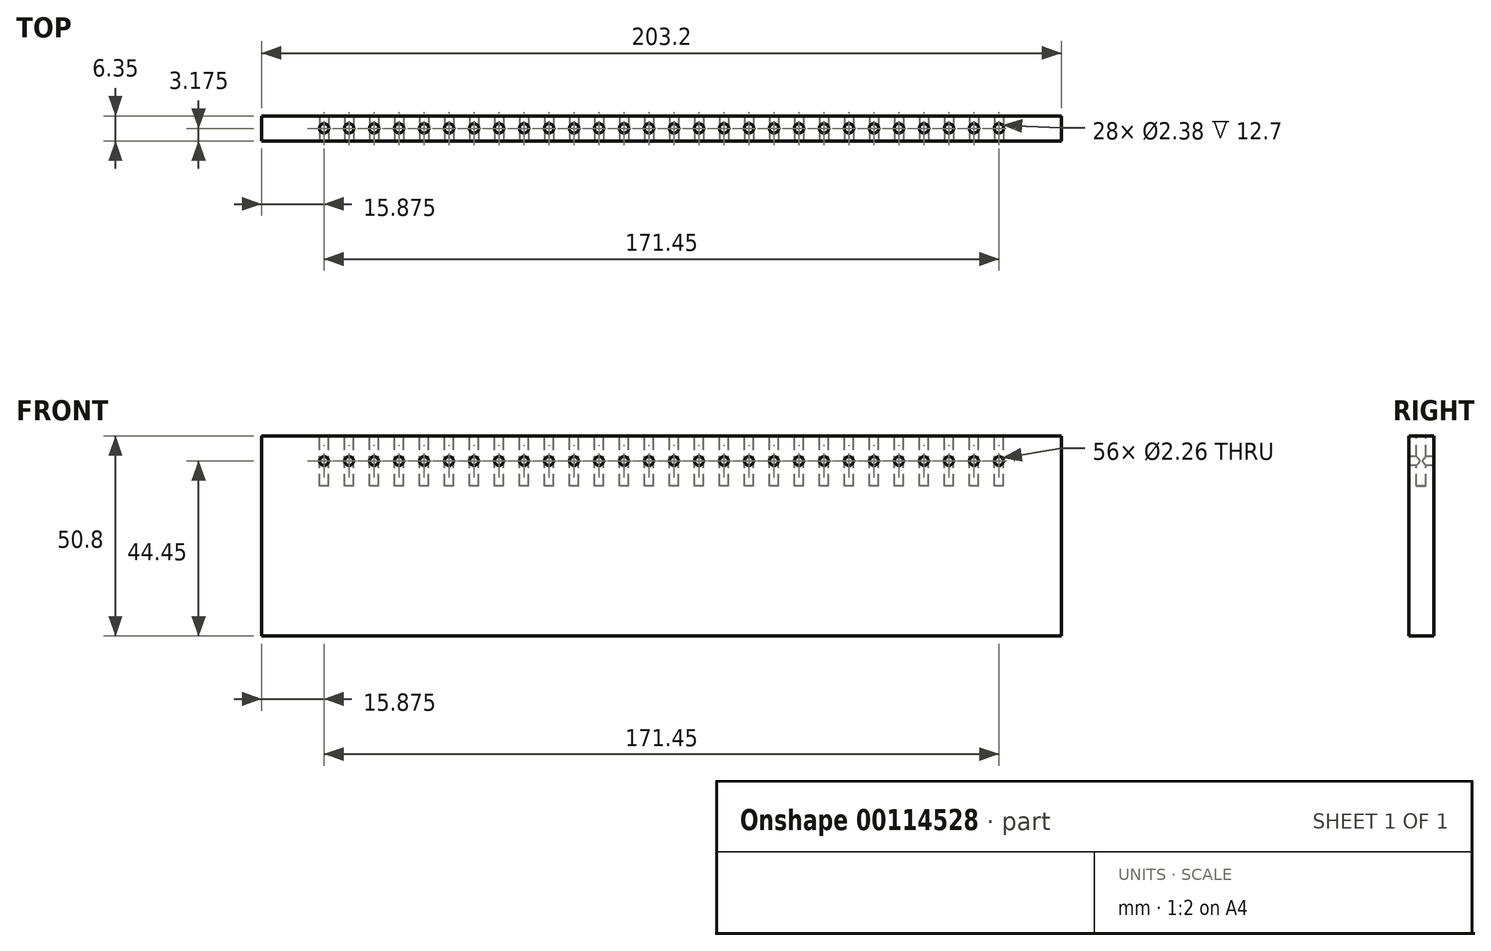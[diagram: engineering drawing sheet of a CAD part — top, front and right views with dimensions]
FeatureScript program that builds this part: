
annotation { "Feature Type Name" : "Feature", "Feature Type Description" : "" }
export const myFeature = defineFeature(function(context is Context, id is Id, definition is map)
    precondition{}
    {
        {
            var Q0;
            Q0=qCreatedBy(makeId("Front.planeOp"),FACE);
            var sketch = newSketch(context, id + "F0", { "sketchPlane" : qUnion([Q0])});
            skLineSegment(sketch, "E0.bottom", {"start": v(0, 0) * mm, "end": v(203.2, 0) * mm});
            skLineSegment(sketch, "E0.top", {"start": v(0, 50.8) * mm, "end": v(203.2, 50.8) * mm});
            skLineSegment(sketch, "E0.left", {"start": v(0, 0) * mm, "end": v(0, 50.8) * mm});
            skLineSegment(sketch, "E0.right", {"start": v(203.2, 0) * mm, "end": v(203.2, 50.8) * mm});
            skSolve(sketch);
        }
        {
            var Q0;
            Q0 = qSketchRegion(id + "F0", true);
            extrude(context, id + "F1", {"entities" : qUnion([Q0]), "depth" : 6.35 * mm});
        }
        {
            var Q0;
            Q0=makeQuery(id+"F1.opExtrude","SWEPT_FACE",FACE,{"disambiguationData":[OSD([sQuery(id+"F0.wireOp",EDGE,"E0.top")])]});
            var sketch = newSketch(context, id + "F2", { "sketchPlane" : qUnion([Q0])});
            skCircle(sketch, "E1", {"center": v(15.88, -3.18) * mm, "radius": 1.2 * mm});
            skCircle(sketch, "E2.1.0.0", {"center": v(22.23, -3.17) * mm, "radius": 1.2 * mm});
            skCircle(sketch, "E2.2.0.0", {"center": v(28.58, -3.18) * mm, "radius": 1.2 * mm});
            skCircle(sketch, "E2.3.0.0", {"center": v(34.92, -3.18) * mm, "radius": 1.2 * mm});
            skCircle(sketch, "E2.4.0.0", {"center": v(41.28, -3.18) * mm, "radius": 1.2 * mm});
            skCircle(sketch, "E2.5.0.0", {"center": v(47.62, -3.18) * mm, "radius": 1.2 * mm});
            skCircle(sketch, "E2.6.0.0", {"center": v(53.98, -3.18) * mm, "radius": 1.2 * mm});
            skCircle(sketch, "E2.7.0.0", {"center": v(60.33, -3.18) * mm, "radius": 1.2 * mm});
            skCircle(sketch, "E2.8.0.0", {"center": v(66.68, -3.18) * mm, "radius": 1.2 * mm});
            skCircle(sketch, "E2.9.0.0", {"center": v(73.03, -3.18) * mm, "radius": 1.2 * mm});
            skCircle(sketch, "E2.10.0.0", {"center": v(79.38, -3.18) * mm, "radius": 1.2 * mm});
            skCircle(sketch, "E2.11.0.0", {"center": v(85.73, -3.18) * mm, "radius": 1.2 * mm});
            skCircle(sketch, "E2.12.0.0", {"center": v(92.08, -3.18) * mm, "radius": 1.2 * mm});
            skCircle(sketch, "E2.13.0.0", {"center": v(98.43, -3.18) * mm, "radius": 1.2 * mm});
            skCircle(sketch, "E2.14.0.0", {"center": v(104.78, -3.18) * mm, "radius": 1.2 * mm});
            skCircle(sketch, "E2.15.0.0", {"center": v(111.13, -3.18) * mm, "radius": 1.2 * mm});
            skCircle(sketch, "E2.16.0.0", {"center": v(117.48, -3.18) * mm, "radius": 1.2 * mm});
            skCircle(sketch, "E2.17.0.0", {"center": v(123.83, -3.18) * mm, "radius": 1.2 * mm});
            skCircle(sketch, "E2.18.0.0", {"center": v(130.18, -3.18) * mm, "radius": 1.2 * mm});
            skCircle(sketch, "E2.19.0.0", {"center": v(136.53, -3.18) * mm, "radius": 1.2 * mm});
            skCircle(sketch, "E2.20.0.0", {"center": v(142.88, -3.18) * mm, "radius": 1.2 * mm});
            skCircle(sketch, "E2.21.0.0", {"center": v(149.23, -3.18) * mm, "radius": 1.2 * mm});
            skCircle(sketch, "E2.22.0.0", {"center": v(155.58, -3.18) * mm, "radius": 1.2 * mm});
            skCircle(sketch, "E2.23.0.0", {"center": v(161.93, -3.18) * mm, "radius": 1.2 * mm});
            skCircle(sketch, "E2.24.0.0", {"center": v(168.28, -3.18) * mm, "radius": 1.2 * mm});
            skCircle(sketch, "E2.25.0.0", {"center": v(174.62, -3.18) * mm, "radius": 1.2 * mm});
            skCircle(sketch, "E2.26.0.0", {"center": v(180.98, -3.18) * mm, "radius": 1.2 * mm});
            skCircle(sketch, "E2.27.0.0", {"center": v(187.33, -3.18) * mm, "radius": 1.2 * mm});
            skLineSegment(sketch, "E2.direction1", {"start": v(15.88, -3.18) * mm, "end": v(22.23, -3.18) * mm, "construction": true});
            skSolve(sketch);
        }
        {
            var Q0;
            Q0 = qSketchRegion(id + "F2", true);
            extrude(context, id + "F3", {"entities" : qUnion([Q0]), "operationType" : NewBodyOperationType.REMOVE, "oppositeDirection" : true, "depth" : 12.7 * mm});
        }
        {
            var Q0;
            Q0=makeQuery(id+"F1.opExtrude","CAP_FACE",FACE,{"disambiguationData":[OSD([sQuery(id+"F0.wireOp",EDGE,"E0.bottom"),sQuery(id+"F0.wireOp",EDGE,"E0.top"),sQuery(id+"F0.wireOp",EDGE,"E0.left"),sQuery(id+"F0.wireOp",EDGE,"E0.right")])],"isStart":false});
            var sketch = newSketch(context, id + "F4", { "sketchPlane" : qUnion([Q0])});
            skPoint(sketch, "E3", {"position": v(15.88, 44.45) * mm});
            skPoint(sketch, "E4.1.0.0", {"position": v(22.22, 44.45) * mm});
            skPoint(sketch, "E4.2.0.0", {"position": v(28.57, 44.45) * mm});
            skPoint(sketch, "E4.3.0.0", {"position": v(34.92, 44.45) * mm});
            skPoint(sketch, "E4.4.0.0", {"position": v(41.27, 44.45) * mm});
            skPoint(sketch, "E4.5.0.0", {"position": v(47.62, 44.45) * mm});
            skPoint(sketch, "E4.6.0.0", {"position": v(53.97, 44.45) * mm});
            skPoint(sketch, "E4.7.0.0", {"position": v(60.32, 44.45) * mm});
            skPoint(sketch, "E4.8.0.0", {"position": v(66.67, 44.45) * mm});
            skPoint(sketch, "E4.9.0.0", {"position": v(73.02, 44.45) * mm});
            skPoint(sketch, "E4.10.0.0", {"position": v(79.37, 44.45) * mm});
            skPoint(sketch, "E4.11.0.0", {"position": v(85.72, 44.45) * mm});
            skPoint(sketch, "E4.12.0.0", {"position": v(92.07, 44.45) * mm});
            skPoint(sketch, "E4.13.0.0", {"position": v(98.42, 44.45) * mm});
            skPoint(sketch, "E4.14.0.0", {"position": v(104.77, 44.45) * mm});
            skPoint(sketch, "E4.15.0.0", {"position": v(111.12, 44.45) * mm});
            skPoint(sketch, "E4.16.0.0", {"position": v(117.47, 44.45) * mm});
            skPoint(sketch, "E4.17.0.0", {"position": v(123.82, 44.45) * mm});
            skPoint(sketch, "E4.18.0.0", {"position": v(130.17, 44.45) * mm});
            skPoint(sketch, "E4.19.0.0", {"position": v(136.52, 44.45) * mm});
            skPoint(sketch, "E4.20.0.0", {"position": v(142.87, 44.45) * mm});
            skPoint(sketch, "E4.21.0.0", {"position": v(149.22, 44.45) * mm});
            skPoint(sketch, "E4.22.0.0", {"position": v(155.57, 44.45) * mm});
            skPoint(sketch, "E4.23.0.0", {"position": v(161.92, 44.45) * mm});
            skPoint(sketch, "E4.24.0.0", {"position": v(168.27, 44.45) * mm});
            skPoint(sketch, "E4.25.0.0", {"position": v(174.62, 44.45) * mm});
            skPoint(sketch, "E4.26.0.0", {"position": v(180.97, 44.45) * mm});
            skPoint(sketch, "E4.27.0.0", {"position": v(187.32, 44.45) * mm});
            skLineSegment(sketch, "E4.direction1", {"start": v(15.88, 44.45) * mm, "end": v(22.22, 44.45) * mm, "construction": true});
            skSolve(sketch);
        }
        {
            var Q0;
            Q0=sQuery(id+"F4.wireOp",VERTEX,"E3");
            var Q1;
            Q1=sQuery(id+"F4.wireOp",VERTEX,"E4.1.0.0");
            var Q2;
            Q2=sQuery(id+"F4.wireOp",VERTEX,"E4.2.0.0");
            var Q3;
            Q3=sQuery(id+"F4.wireOp",VERTEX,"E4.3.0.0");
            var Q4;
            Q4=sQuery(id+"F4.wireOp",VERTEX,"E4.4.0.0");
            var Q5;
            Q5=sQuery(id+"F4.wireOp",VERTEX,"E4.5.0.0");
            var Q6;
            Q6=sQuery(id+"F4.wireOp",VERTEX,"E4.6.0.0");
            var Q7;
            Q7=sQuery(id+"F4.wireOp",VERTEX,"E4.7.0.0");
            var Q8;
            Q8=sQuery(id+"F4.wireOp",VERTEX,"E4.8.0.0");
            var Q9;
            Q9=sQuery(id+"F4.wireOp",VERTEX,"E4.9.0.0");
            var Q10;
            Q10=sQuery(id+"F4.wireOp",VERTEX,"E4.10.0.0");
            var Q11;
            Q11=sQuery(id+"F4.wireOp",VERTEX,"E4.11.0.0");
            var Q12;
            Q12=sQuery(id+"F4.wireOp",VERTEX,"E4.12.0.0");
            var Q13;
            Q13=sQuery(id+"F4.wireOp",VERTEX,"E4.13.0.0");
            var Q14;
            Q14=sQuery(id+"F4.wireOp",VERTEX,"E4.14.0.0");
            var Q15;
            Q15=sQuery(id+"F4.wireOp",VERTEX,"E4.15.0.0");
            var Q16;
            Q16=sQuery(id+"F4.wireOp",VERTEX,"E4.16.0.0");
            var Q17;
            Q17=sQuery(id+"F4.wireOp",VERTEX,"E4.21.0.0");
            var Q18;
            Q18=sQuery(id+"F4.wireOp",VERTEX,"E4.26.0.0");
            var Q19;
            Q19=sQuery(id+"F4.wireOp",VERTEX,"E4.25.0.0");
            var Q20;
            Q20=sQuery(id+"F4.wireOp",VERTEX,"E4.24.0.0");
            var Q21;
            Q21=sQuery(id+"F4.wireOp",VERTEX,"E4.23.0.0");
            var Q22;
            Q22=sQuery(id+"F4.wireOp",VERTEX,"E4.22.0.0");
            var Q23;
            Q23=sQuery(id+"F4.wireOp",VERTEX,"E4.20.0.0");
            var Q24;
            Q24=sQuery(id+"F4.wireOp",VERTEX,"E4.19.0.0");
            var Q25;
            Q25=sQuery(id+"F4.wireOp",VERTEX,"E4.18.0.0");
            var Q26;
            Q26=sQuery(id+"F4.wireOp",VERTEX,"E4.17.0.0");
            var Q27;
            Q27=sQuery(id+"F4.wireOp",VERTEX,"E4.27.0.0");
            var Q28;
            Q28=makeQuery(id+"F1.opExtrude","SWEPT_BODY",BODY,{"disambiguationData":[OSD([sQuery(id+"F0.wireOp",EDGE,"E0.bottom"),sQuery(id+"F0.wireOp",EDGE,"E0.top"),sQuery(id+"F0.wireOp",EDGE,"E0.left"),sQuery(id+"F0.wireOp",EDGE,"E0.right")])]});
            hole(context, id + "F5", {"style" : HoleStyle.SIMPLE, "endStyle" : HoleEndStyle.THROUGH, "standardTappedOrClearance" : lookupTablePath({ "standard" : "ANSI", "engagement" : "75%", "pitch" : "40 tpi", "size" : "#4", "type" : "Tapped" }), "standardBlindInLast" : lookupTablePath({ "standard" : "ANSI", "engagement" : "75%", "pitch" : "40 tpi", "size" : "#4", "type" : "Tapped" }), "holeDiameter" : 2.26 * mm, "locations" : qUnion([Q0, Q1, Q2, Q3, Q4, Q5, Q6, Q7, Q8, Q9, Q10, Q11, Q12, Q13, Q14, Q15, Q16, Q17, Q18, Q19, Q20, Q21, Q22, Q23, Q24, Q25, Q26, Q27]), "scope" : qUnion([Q28]), "isTappedThrough" : true, "majorDiameter" : 2.84 * mm, "showTappedDepth" : true});
        }
    });
